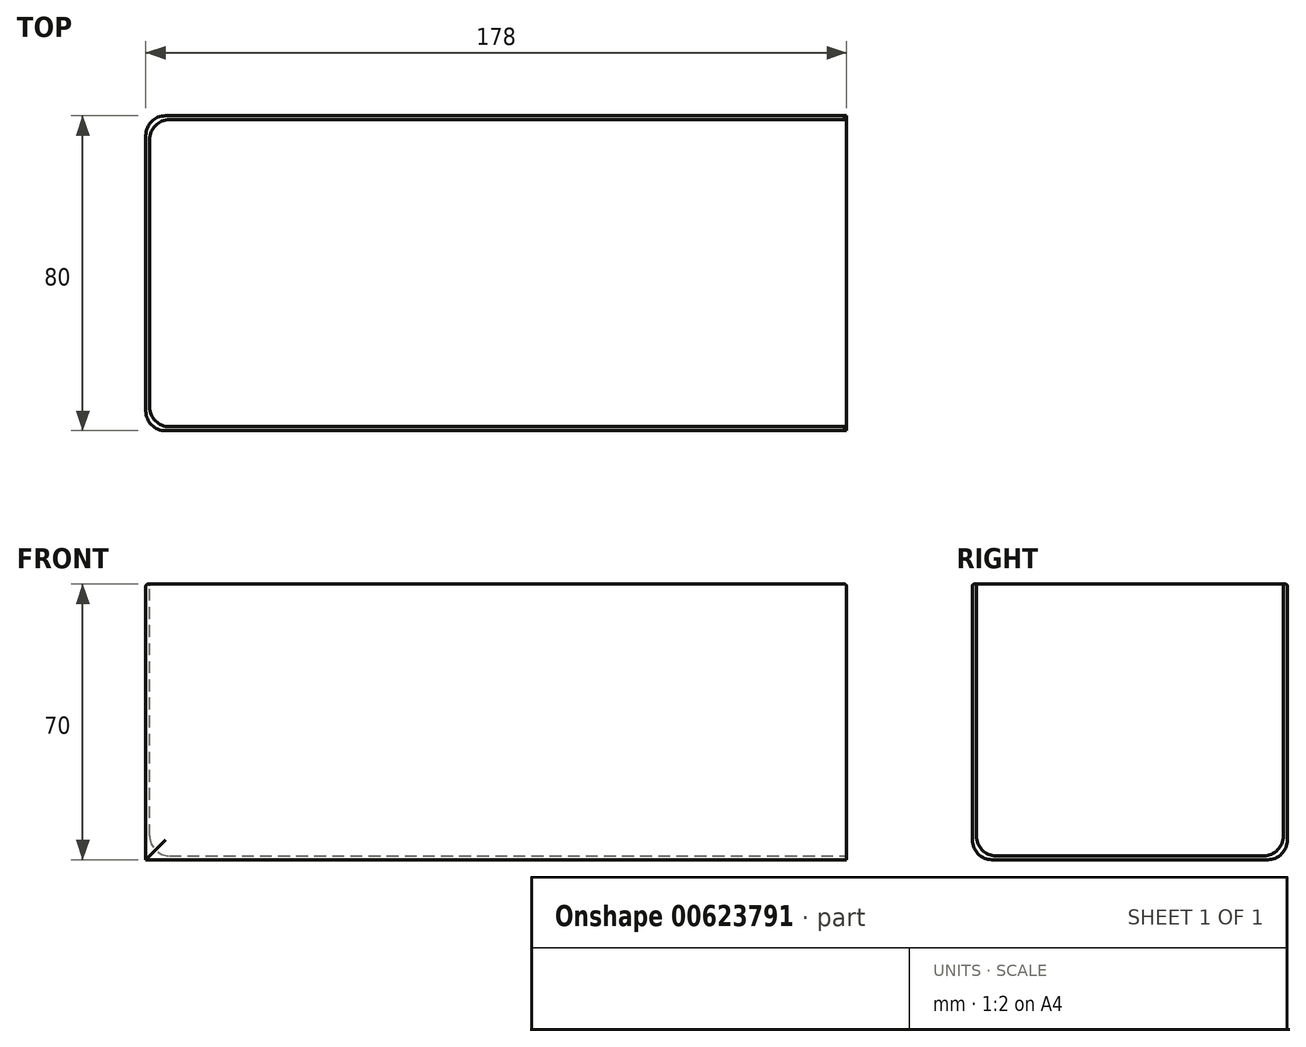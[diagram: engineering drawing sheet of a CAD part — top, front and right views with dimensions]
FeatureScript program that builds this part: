
annotation { "Feature Type Name" : "Feature", "Feature Type Description" : "" }
export const myFeature = defineFeature(function(context is Context, id is Id, definition is map)
    precondition{}
    {
        {
            var Q0;
            Q0=qCreatedBy(makeId("Top.planeOp"),FACE);
            var sketch = newSketch(context, id + "F0", { "sketchPlane" : qUnion([Q0])});
            skLineSegment(sketch, "E0.bottom", {"start": v(89, -40) * mm, "end": v(-89, -40) * mm});
            skLineSegment(sketch, "E0.top", {"start": v(89, 40) * mm, "end": v(-89, 40) * mm});
            skLineSegment(sketch, "E0.left", {"start": v(89, -40) * mm, "end": v(89, 40) * mm});
            skLineSegment(sketch, "E0.right", {"start": v(-89, -40) * mm, "end": v(-89, 40) * mm});
            skPoint(sketch, "E0.middle", {"position": v(0, 0) * mm});
            skSolve(sketch);
        }
        {
            var Q0;
            Q0=makeQuery(id+"F0.imprint","IMPRINT",FACE,{"disambiguationData":[TD([[makeQuery(id+"F0.imprint","IMPRINT",EDGE,{"derivedFrom":sQuery(id+"F0.wireOp",EDGE,"E0.bottom")}),-1.0]])]});
            extrude(context, id + "F1", {"entities" : qUnion([Q0]), "depth" : 70 * mm, "offsetDistance" : 25 * mm});
        }
        {
            var Q0;
            Q0=makeQuery(id+"F1.opExtrude","CAP_FACE",FACE,{"disambiguationData":[OSD([sQuery(id+"F0.wireOp",EDGE,"E0.bottom"),sQuery(id+"F0.wireOp",EDGE,"E0.top"),sQuery(id+"F0.wireOp",EDGE,"E0.left"),sQuery(id+"F0.wireOp",EDGE,"E0.right")])],"isStart":false});
            var sketch = newSketch(context, id + "F2", { "sketchPlane" : qUnion([Q0])});
            skLineSegment(sketch, "E1.bottom", {"start": v(-88, -39) * mm, "end": v(89, -39) * mm});
            skLineSegment(sketch, "E1.top", {"start": v(-88, 39) * mm, "end": v(89, 39) * mm});
            skLineSegment(sketch, "E1.left", {"start": v(-88, -39) * mm, "end": v(-88, 39) * mm});
            skLineSegment(sketch, "E1.right", {"start": v(89, -39) * mm, "end": v(89, 39) * mm});
            skLineSegment(sketch, "E2", {"start": v(-89, -24.02) * mm, "end": v(-88, -24.02) * mm});
            skLineSegment(sketch, "E3", {"start": v(-83, -39) * mm, "end": v(-83, -40) * mm});
            skSolve(sketch);
        }
        {
            var Q0;
            {var subQ4=sQuery(id+"F2.wireOp",EDGE,"E1.top");Q0=makeQuery(id+"F2.imprint","IMPRINT",FACE,{"disambiguationData":[TD([[makeQuery(id+"F2.imprint","IMPRINT",EDGE,{"derivedFrom":subQ4}),-1.0]])]});}
            extrude(context, id + "F3", {"entities" : qUnion([Q0]), "operationType" : NewBodyOperationType.REMOVE, "oppositeDirection" : true, "depth" : 69 * mm, "offsetDistance" : 25 * mm});
        }
        {
            var Q0;
            Q0=makeQuery(id+"F3.boolean.opBoolean","COPY",EDGE,{"derivedFrom":makeQuery(id+"F3.opExtrude","SWEPT_EDGE",EDGE,{"disambiguationData":[OSD([sQuery(id+"F2.wireOp",EDGE,"E1.top"),sQuery(id+"F2.wireOp",EDGE,"E1.left")])]})});
            var Q1;
            Q1=makeQuery(id+"F3.boolean.opBoolean","COPY",EDGE,{"derivedFrom":makeQuery(id+"F3.opExtrude","CAP_EDGE",EDGE,{"disambiguationData":[OSD([sQuery(id+"F2.wireOp",EDGE,"E1.top")])],"isStart":false})});
            var Q2;
            Q2=makeQuery(id+"F3.boolean.opBoolean","COPY",EDGE,{"derivedFrom":makeQuery(id+"F3.opExtrude","CAP_EDGE",EDGE,{"disambiguationData":[OSD([sQuery(id+"F2.wireOp",EDGE,"E1.left")])],"isStart":false})});
            var Q3;
            Q3=makeQuery(id+"F3.boolean.opBoolean","COPY",EDGE,{"derivedFrom":makeQuery(id+"F3.opExtrude","SWEPT_EDGE",EDGE,{"disambiguationData":[OSD([sQuery(id+"F2.wireOp",EDGE,"E1.bottom"),sQuery(id+"F2.wireOp",EDGE,"E1.left")])]})});
            var Q4;
            Q4=makeQuery(id+"F3.boolean.opBoolean","COPY",EDGE,{"derivedFrom":makeQuery(id+"F3.opExtrude","CAP_EDGE",EDGE,{"disambiguationData":[OSD([sQuery(id+"F2.wireOp",EDGE,"E1.bottom")])],"isStart":false})});
            var Q5;
            Q5=makeQuery(id+"F1.opExtrude","CAP_EDGE",EDGE,{"disambiguationData":[OSD([sQuery(id+"F0.wireOp",EDGE,"E0.top")])],"isStart":true});
            var Q6;
            Q6=makeQuery(id+"F1.opExtrude","SWEPT_EDGE",EDGE,{"disambiguationData":[OSD([sQuery(id+"F0.wireOp",EDGE,"E0.top"),sQuery(id+"F0.wireOp",EDGE,"E0.right")])]});
            var Q7;
            Q7=makeQuery(id+"F1.opExtrude","SWEPT_EDGE",EDGE,{"disambiguationData":[OSD([sQuery(id+"F0.wireOp",EDGE,"E0.bottom"),sQuery(id+"F0.wireOp",EDGE,"E0.right")])]});
            var Q8;
            Q8=makeQuery(id+"F1.opExtrude","CAP_EDGE",EDGE,{"disambiguationData":[OSD([sQuery(id+"F0.wireOp",EDGE,"E0.bottom")])],"isStart":true});
            fillet(context, id + "F4", {"entities" : qUnion([Q0, Q1, Q2, Q3, Q4, Q5, Q6, Q7, Q8]), "radius" : 5 * mm, "tangentPropagation" : true, "allowEdgeOverflow" : false});
        }
        {
            var Q0;
            Q0=makeQuery(id+"F1.opExtrude","CAP_FACE",FACE,{"disambiguationData":[OSD([sQuery(id+"F0.wireOp",EDGE,"E0.bottom"),sQuery(id+"F0.wireOp",EDGE,"E0.top"),sQuery(id+"F0.wireOp",EDGE,"E0.left"),sQuery(id+"F0.wireOp",EDGE,"E0.right")])],"isStart":false});
            fillet(context, id + "F5", {"entities" : qUnion([Q0]), "radius" : .5 * mm, "tangentPropagation" : true, "allowEdgeOverflow" : false});
        }
    });
